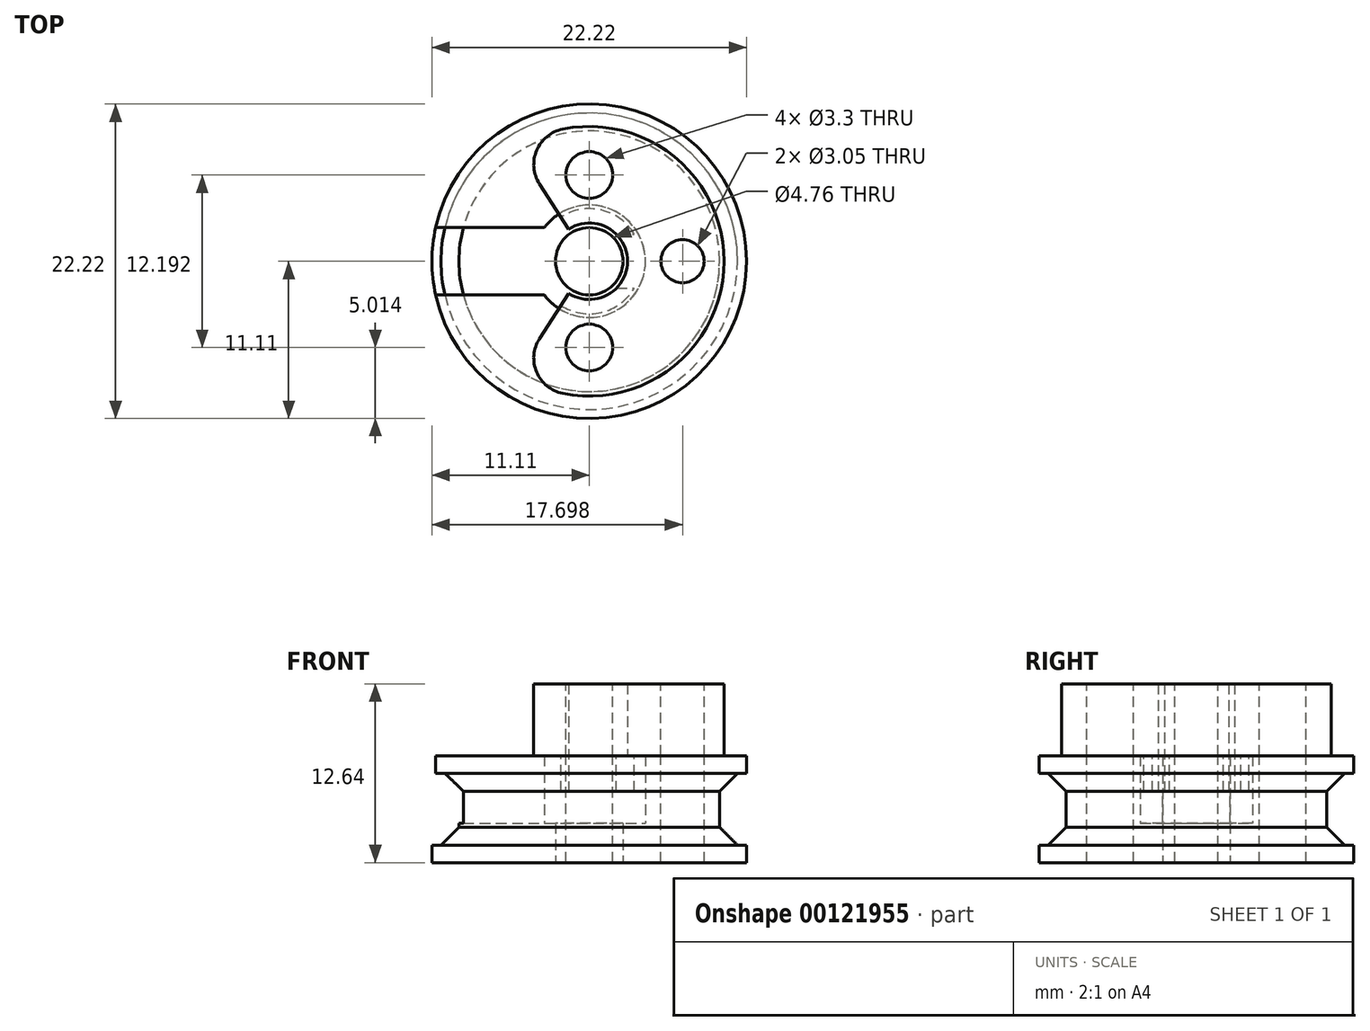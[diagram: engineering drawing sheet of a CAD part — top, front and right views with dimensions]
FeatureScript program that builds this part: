
annotation { "Feature Type Name" : "Feature", "Feature Type Description" : "" }
export const myFeature = defineFeature(function(context is Context, id is Id, definition is map)
    precondition{}
    {
        {
            var Q0;
            Q0=qCreatedBy(makeId("Top.planeOp"),FACE);
            var sketch = newSketch(context, id + "F0", { "sketchPlane" : qUnion([Q0])});
            skCircle(sketch, "E0", {"center": v(0, 0) * mm, "radius": 11.11 * mm});
            skSolve(sketch);
        }
        {
            var Q0;
            Q0 = qSketchRegion(id + "F0", true);
            extrude(context, id + "F1", {"entities" : qUnion([Q0]), "depth" : 1.27 * mm});
        }
        {
            var Q0;
            Q0=makeQuery(id+"F1.opExtrude","CAP_FACE",FACE,{"disambiguationData":[OSD([sQuery(id+"F0.wireOp",EDGE,"E0")])],"isStart":false});
            var sketch = newSketch(context, id + "F2", { "sketchPlane" : qUnion([Q0])});
            skCircle(sketch, "E1", {"center": v(0, 0) * mm, "radius": 2.38 * mm});
            skCircle(sketch, "E2.0", {"center": v(0, 0) * mm, "radius": 11.11 * mm});
            skSolve(sketch);
        }
        {
            var Q0;
            Q0 = qSketchRegion(id + "F2", true);
            extrude(context, id + "F3", {"entities" : qUnion([Q0]), "operationType" : NewBodyOperationType.ADD, "depth" : 1.52 * mm});
        }
        {
            var Q0;
            Q0=makeQuery(id+"F3.opExtrude","CAP_FACE",FACE,{"disambiguationData":[OSD([sQuery(id+"F2.wireOp",EDGE,"E1"),sQuery(id+"F2.wireOp",EDGE,"E2.0")])],"isStart":false});
            var sketch = newSketch(context, id + "F4", { "sketchPlane" : qUnion([Q0])});
            skCircle(sketch, "E3", {"center": v(0, 0) * mm, "radius": 3.97 * mm});
            skCircle(sketch, "E4.0", {"center": v(0, 0) * mm, "radius": 11.11 * mm});
            skSolve(sketch);
        }
        {
            var Q0;
            Q0 = qSketchRegion(id + "F4", true);
            extrude(context, id + "F5", {"entities" : qUnion([Q0]), "operationType" : NewBodyOperationType.ADD, "depth" : 4.76 * mm});
        }
        {
            var Q0;
            Q0=qCreatedBy(makeId("Right.planeOp"),FACE);
            var sketch = newSketch(context, id + "F6", { "sketchPlane" : qUnion([Q0])});
            skLineSegment(sketch, "E5", {"start": v(11.11, 7.56) * mm, "end": v(11.11, 0) * mm, "construction": true});
            skLineSegment(sketch, "E6", {"start": v(11.11, 6.32) * mm, "end": v(9.2, 6.32) * mm});
            skLineSegment(sketch, "E7", {"start": v(9.2, 6.32) * mm, "end": v(9.2, 1.24) * mm});
            skLineSegment(sketch, "E8", {"start": v(9.2, 1.24) * mm, "end": v(11.11, 1.24) * mm});
            skLineSegment(sketch, "E9", {"start": v(11.11, 1.24) * mm, "end": v(11.11, 6.32) * mm});
            skLineSegment(sketch, "E10", {"start": v(0, 0) * mm, "end": v(0, 7.56) * mm, "construction": true});
            skLineSegment(sketch, "E11", {"start": v(9.2, 3.78) * mm, "end": v(0, 3.78) * mm, "construction": true});
            skSolve(sketch);
        }
        {
            var Q0;
            Q0 = qSketchRegion(id + "F6", true);
            var Q1;
            Q1=sQuery(id+"F6.wireOp",EDGE,"E10");
            revolve(context, id + "F7", {"operationType" : NewBodyOperationType.REMOVE, "entities" : qUnion([Q0]), "axis" : qUnion([Q1]), "revolveType" : RevolveType.FULL, "oppositeDirection" : true});
        }
        {
            var Q0;
            Q0=makeQuery(id+"F7.boolean.opBoolean","COPY",EDGE,{"derivedFrom":makeQuery(id+"F7.opRevolve","SWEPT_EDGE",EDGE,{"disambiguationData":[OSD([sQuery(id+"F6.wireOp",EDGE,"E7"),sQuery(id+"F6.wireOp",EDGE,"E8")])]})});
            var Q1;
            Q1=makeQuery(id+"F7.boolean.opBoolean","COPY",EDGE,{"derivedFrom":makeQuery(id+"F7.opRevolve","SWEPT_EDGE",EDGE,{"disambiguationData":[OSD([sQuery(id+"F6.wireOp",EDGE,"E6"),sQuery(id+"F6.wireOp",EDGE,"E7")])]})});
            chamfer(context, id + "F8", {"entities" : qUnion([Q0, Q1]), "width" : 1.27 * mm, "tangentPropagation" : true});
        }
        {
            var Q0;
            Q0=qCreatedBy(makeId("Right.planeOp"),FACE);
            var sketch = newSketch(context, id + "F9", { "sketchPlane" : qUnion([Q0])});
            skLineSegment(sketch, "E12.bottom", {"start": v(-2.38, 5.05) * mm, "end": v(2.38, 5.05) * mm});
            skLineSegment(sketch, "E13", {"start": v(0, 5.05) * mm, "end": v(0, 0) * mm, "construction": true});
            skLineSegment(sketch, "E14.0", {"start": v(-3.97, 2.8) * mm, "end": v(3.97, 2.8) * mm});
            skLineSegment(sketch, "E15", {"start": v(2.38, 5.05) * mm, "end": v(2.38, 2.8) * mm});
            skLineSegment(sketch, "E16", {"start": v(-2.38, 5.05) * mm, "end": v(-2.38, 2.8) * mm});
            skSolve(sketch);
        }
        {
            var Q0;
            Q0 = qSketchRegion(id + "F9", true);
            extrude(context, id + "F10", {"entities" : qUnion([Q0]), "operationType" : NewBodyOperationType.REMOVE, "oppositeDirection" : true, "depth" : 25.4 * mm});
        }
        {
            var Q0;
            Q0=makeQuery(id+"F5.opExtrude","CAP_FACE",FACE,{"disambiguationData":[OSD([sQuery(id+"F4.wireOp",EDGE,"E3"),sQuery(id+"F4.wireOp",EDGE,"E4.0")])],"isStart":false});
            var sketch = newSketch(context, id + "F11", { "sketchPlane" : qUnion([Q0])});
            skArc(sketch, "E17.0", {"start": v(-8.9, 2.38) * mm, "mid": v(9.2, 0) * mm, "end": v(-8.9, -2.38) * mm, "construction": true});
            skArc(sketch, "E17.1", {"start": v(-3.18, -2.38) * mm, "mid": v(3.97, 0) * mm, "end": v(-3.17, 2.38) * mm, "construction": true});
            skLineSegment(sketch, "E18", {"start": v(3.97, 0) * mm, "end": v(9.2, 0) * mm, "construction": true});
            skCircle(sketch, "E19", {"center": v(6.59, 0) * mm, "radius": 1.22 * mm});
            skSolve(sketch);
        }
        {
            var Q0;
            Q0 = qSketchRegion(id + "F11", true);
            extrude(context, id + "F12", {"entities" : qUnion([Q0]), "operationType" : NewBodyOperationType.REMOVE, "endBound" : BoundingType.THROUGH_ALL, "oppositeDirection" : true, "depth" : 25.4 * mm});
        }
        {
            var Q0;
            Q0=makeQuery(id+"F5.opExtrude","CAP_FACE",FACE,{"disambiguationData":[OSD([sQuery(id+"F4.wireOp",EDGE,"E3"),sQuery(id+"F4.wireOp",EDGE,"E4.0")])],"isStart":false});
            var sketch = newSketch(context, id + "F13", { "sketchPlane" : qUnion([Q0])});
            skArc(sketch, "E20", {"start": v(-1.46, -2.27) * mm, "mid": v(2.7, 0) * mm, "end": v(-1.46, 2.27) * mm});
            skArc(sketch, "E21", {"start": v(-5.15, -8.01) * mm, "mid": v(9.53, 0) * mm, "end": v(-5.15, 8.01) * mm});
            skLineSegment(sketch, "E22", {"start": v(-1.46, 2.27) * mm, "end": v(-5.15, 8.01) * mm});
            skLineSegment(sketch, "E23", {"start": v(-1.46, -2.27) * mm, "end": v(-5.15, -8.01) * mm});
            skCircle(sketch, "E24.0", {"center": v(6.59, 0) * mm, "radius": 1.22 * mm});
            skSolve(sketch);
        }
        {
            var Q0;
            Q0 = qSketchRegion(id + "F13", true);
            extrude(context, id + "F14", {"entities" : qUnion([Q0]), "depth" : 5.08 * mm});
        }
        {
            var Q0;
            Q0=makeQuery(id+"F14.opExtrude","SWEPT_EDGE",EDGE,{"disambiguationData":[OSD([sQuery(id+"F13.wireOp",EDGE,"E21"),sQuery(id+"F13.wireOp",EDGE,"E22")])]});
            var Q1;
            Q1=makeQuery(id+"F14.opExtrude","SWEPT_EDGE",EDGE,{"disambiguationData":[OSD([sQuery(id+"F13.wireOp",EDGE,"E21"),sQuery(id+"F13.wireOp",EDGE,"E23")])]});
            fillet(context, id + "F15", {"entities" : qUnion([Q0, Q1]), "radius" : 2.54 * mm, "tangentPropagation" : true, "allowEdgeOverflow" : false});
        }
        {
            var Q0;
            Q0=makeQuery(id+"F14.opExtrude","CAP_FACE",FACE,{"disambiguationData":[OSD([sQuery(id+"F13.wireOp",EDGE,"E20"),sQuery(id+"F13.wireOp",EDGE,"E21"),sQuery(id+"F13.wireOp",EDGE,"E22"),sQuery(id+"F13.wireOp",EDGE,"E23"),sQuery(id+"F13.wireOp",EDGE,"E24.0")])],"isStart":true});
            var sketch = newSketch(context, id + "F16", { "sketchPlane" : qUnion([Q0])});
            skCircle(sketch, "E25.0", {"center": v(0, 0) * mm, "radius": 3.97 * mm, "construction": true});
            skArc(sketch, "E26.0", {"start": v(-2, -3.12) * mm, "mid": v(0.85, -3.62) * mm, "end": v(3.19, -1.9) * mm});
            skLineSegment(sketch, "E27", {"start": v(1.91, -1.9) * mm, "end": v(3.19, -1.9) * mm});
            skLineSegment(sketch, "E28", {"start": v(1.91, 1.9) * mm, "end": v(3.19, 1.9) * mm});
            skArc(sketch, "E29.0", {"start": v(-1.46, 2.27) * mm, "mid": v(0.3, 2.68) * mm, "end": v(1.91, 1.9) * mm});
            skLineSegment(sketch, "E30", {"start": v(-1.46, -2.27) * mm, "end": v(-2, -3.12) * mm});
            skLineSegment(sketch, "E31", {"start": v(-1.46, 2.27) * mm, "end": v(-2, 3.12) * mm});
            skArc(sketch, "E32.trimOffspring", {"start": v(1.91, -1.9) * mm, "mid": v(0.3, -2.68) * mm, "end": v(-1.46, -2.27) * mm});
            skArc(sketch, "E33.trimOffspring", {"start": v(3.19, 1.9) * mm, "mid": v(0.85, 3.62) * mm, "end": v(-2, 3.12) * mm});
            skSolve(sketch);
        }
        {
            var Q0;
            Q0=makeQuery(id+"F16.imprint","IMPRINT",FACE,{"disambiguationData":[TD([[makeQuery(id+"F16.imprint","IMPRINT",EDGE,{"derivedFrom":sQuery(id+"F16.wireOp",EDGE,"E28")}),1.0]])]});
            var Q1;
            Q1=makeQuery(id+"F16.imprint","IMPRINT",FACE,{"disambiguationData":[TD([[makeQuery(id+"F16.imprint","IMPRINT",EDGE,{"derivedFrom":sQuery(id+"F16.wireOp",EDGE,"E26.0")}),1.0]])]});
            extrude(context, id + "F17", {"entities" : qUnion([Q0, Q1]), "operationType" : NewBodyOperationType.ADD, "depth" : 2.54 * mm});
        }
        {
            var Q0;
            Q0=makeQuery(id+"F14.opExtrude","CAP_FACE",FACE,{"disambiguationData":[OSD([sQuery(id+"F13.wireOp",EDGE,"E20"),sQuery(id+"F13.wireOp",EDGE,"E21"),sQuery(id+"F13.wireOp",EDGE,"E22"),sQuery(id+"F13.wireOp",EDGE,"E23"),sQuery(id+"F13.wireOp",EDGE,"E24.0")])],"isStart":false});
            var sketch = newSketch(context, id + "F18", { "sketchPlane" : qUnion([Q0])});
            skCircle(sketch, "E34.0", {"center": v(6.59, 0) * mm, "radius": 1.52 * mm});
            skSolve(sketch);
        }
        {
            var Q0;
            Q0 = qSketchRegion(id + "F18", true);
            extrude(context, id + "F19", {"entities" : qUnion([Q0]), "operationType" : NewBodyOperationType.REMOVE, "endBound" : BoundingType.THROUGH_ALL, "oppositeDirection" : true, "depth" : 25.4 * mm});
        }
        {
            var Q0;
            Q0=makeQuery(id+"F10.boolean.opBoolean","MERGE",FACE,{"derivedFrom":[makeQuery(id+"F3.opExtrude","CAP_FACE",FACE,{"disambiguationData":[OSD([sQuery(id+"F2.wireOp",EDGE,"E1"),sQuery(id+"F2.wireOp",EDGE,"E2.0")])],"isStart":false}),makeQuery(id+"F10.opExtrude","SWEPT_FACE",FACE,{"disambiguationData":[OSD([sQuery(id+"F9.wireOp",EDGE,"E14.0")])]})]});
            var sketch = newSketch(context, id + "F20", { "sketchPlane" : qUnion([Q0])});
            skLineSegment(sketch, "E35.bottom", {"start": v(-3.17, -2.38) * mm, "end": v(-11.11, -2.38) * mm});
            skLineSegment(sketch, "E35.top", {"start": v(-3.17, 2.38) * mm, "end": v(-11.11, 2.38) * mm});
            skLineSegment(sketch, "E35.left", {"start": v(-3.17, -2.38) * mm, "end": v(-3.17, 2.38) * mm});
            skLineSegment(sketch, "E35.right", {"start": v(-11.11, -2.38) * mm, "end": v(-11.11, 2.38) * mm});
            skSolve(sketch);
        }
        {
            var Q0;
            Q0 = qSketchRegion(id + "F20", true);
            extrude(context, id + "F21", {"entities" : qUnion([Q0]), "operationType" : NewBodyOperationType.REMOVE, "endBound" : BoundingType.THROUGH_ALL, "depth" : 25.4 * mm});
        }
        {
            var Q0;
            Q0=makeQuery(id+"F1.opExtrude","CAP_FACE",FACE,{"disambiguationData":[OSD([sQuery(id+"F0.wireOp",EDGE,"E0")])],"isStart":true});
            var sketch = newSketch(context, id + "F22", { "sketchPlane" : qUnion([Q0])});
            skCircle(sketch, "E36", {"center": v(0, 0) * mm, "radius": 6.1 * mm, "construction": true});
            skCircle(sketch, "E37", {"center": v(0, 6.1) * mm, "radius": 1.22 * mm});
            skCircle(sketch, "E38", {"center": v(0, -6.1) * mm, "radius": 1.22 * mm});
            skSolve(sketch);
        }
        {
            var Q0;
            Q0 = qSketchRegion(id + "F22", true);
            extrude(context, id + "F23", {"entities" : qUnion([Q0]), "operationType" : NewBodyOperationType.REMOVE, "endBound" : BoundingType.THROUGH_ALL, "oppositeDirection" : true, "depth" : 25.4 * mm});
        }
        {
            var Q0;
            Q0=makeQuery(id+"F1.opExtrude","CAP_FACE",FACE,{"disambiguationData":[OSD([sQuery(id+"F0.wireOp",EDGE,"E0")])],"isStart":false});
            var sketch = newSketch(context, id + "F24", { "sketchPlane" : qUnion([Q0])});
            skCircle(sketch, "E39.0.0", {"center": v(0, 0) * mm, "radius": 2.38 * mm});
            skSolve(sketch);
        }
        {
            var Q0;
            Q0 = qSketchRegion(id + "F24", true);
            extrude(context, id + "F25", {"entities" : qUnion([Q0]), "operationType" : NewBodyOperationType.REMOVE, "endBound" : BoundingType.UP_TO_NEXT, "oppositeDirection" : true, "depth" : 25.4 * mm});
        }
        {
            var Q0;
            Q0=makeQuery(id+"F14.opExtrude","CAP_FACE",FACE,{"disambiguationData":[OSD([sQuery(id+"F13.wireOp",EDGE,"E20"),sQuery(id+"F13.wireOp",EDGE,"E21"),sQuery(id+"F13.wireOp",EDGE,"E22"),sQuery(id+"F13.wireOp",EDGE,"E23"),sQuery(id+"F13.wireOp",EDGE,"E24.0")])],"isStart":false});
            var sketch = newSketch(context, id + "F26", { "sketchPlane" : qUnion([Q0])});
            skCircle(sketch, "E40", {"center": v(0, 6.1) * mm, "radius": 1.65 * mm});
            skCircle(sketch, "E41", {"center": v(0, -6.1) * mm, "radius": 1.65 * mm});
            skSolve(sketch);
        }
        {
            var Q0;
            Q0 = qSketchRegion(id + "F26", true);
            extrude(context, id + "F27", {"entities" : qUnion([Q0]), "operationType" : NewBodyOperationType.REMOVE, "endBound" : BoundingType.THROUGH_ALL, "oppositeDirection" : true, "depth" : 25.4 * mm});
        }
    });
